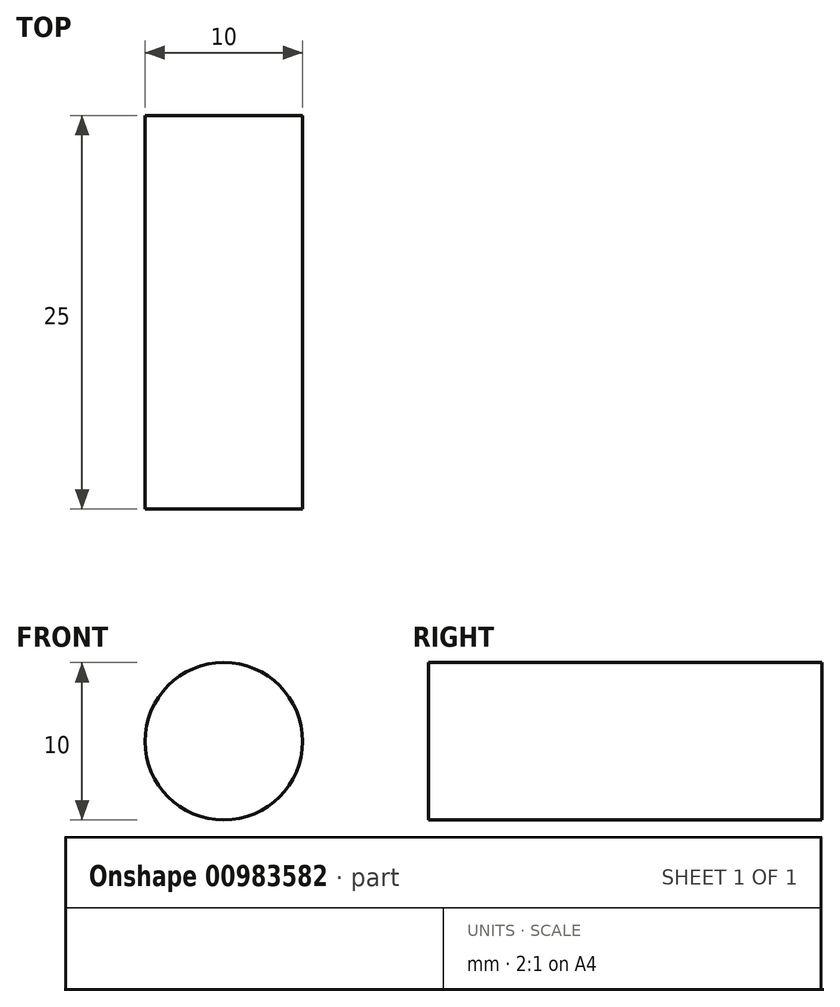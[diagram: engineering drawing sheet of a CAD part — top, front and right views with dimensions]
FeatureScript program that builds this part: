
annotation { "Feature Type Name" : "Feature", "Feature Type Description" : "" }
export const myFeature = defineFeature(function(context is Context, id is Id, definition is map)
    precondition{}
    {
        {
            var Q0;
            Q0=qCreatedBy(makeId("Front.planeOp"),FACE);
            var sketch = newSketch(context, id + "F0", { "sketchPlane" : qUnion([Q0])});
            skCircle(sketch, "E0", {"center": v(0, 0) * mm, "radius": 5 * mm});
            skSolve(sketch);
        }
        {
            var Q0;
            Q0=qSketchRegion(id+"F0",true);
            extrude(context, id + "F1", {"entities" : qUnion([Q0]), "depth" : 25 * mm, "offsetDistance" : 25 * mm});
        }
    });
